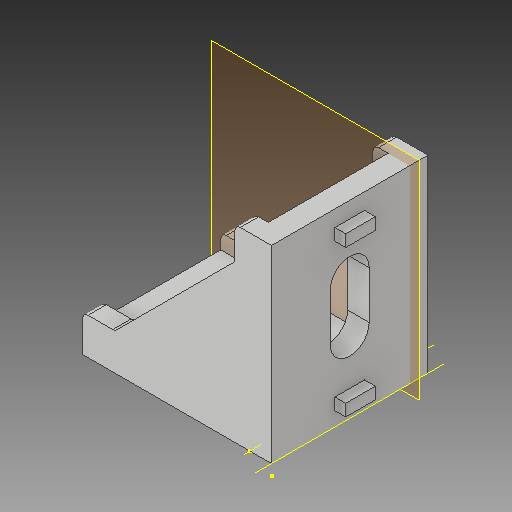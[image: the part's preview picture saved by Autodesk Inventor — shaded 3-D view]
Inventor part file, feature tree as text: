
AUTODESK INVENTOR PART (.ipt)
format: ipt  version: 2018 (Build 220112000, 112)  size: 188,416 bytes
history: native  units: mm
features: sketch x8, other x5, plane x1
ambient origin geometry x8: Origin, YZ Plane, XZ Plane, XY Plane, X Axis, Y Axis, Z Axis, Center Point
bodies: Solid1 (feature_tree)
feature tree (14):
  other  "30mm Bracket_CPY.ipt"
  other  "Solid1::30mm Bracket_CPY.ipt"
  other  "TaggingFeature1"
  sketch  "Sketch1"  dims[d0=10.0mm]
  sketch  "Sketch2"
  sketch  "Sketch3"
  sketch  "Sketch4"
  sketch  "Sketch5"
  sketch  "Sketch7"
  sketch  "Sketch9"
  sketch  "Sketch10"
  plane  "Work Plane1"
  other  "Work Axis1"
  other  "Work Axis2"
